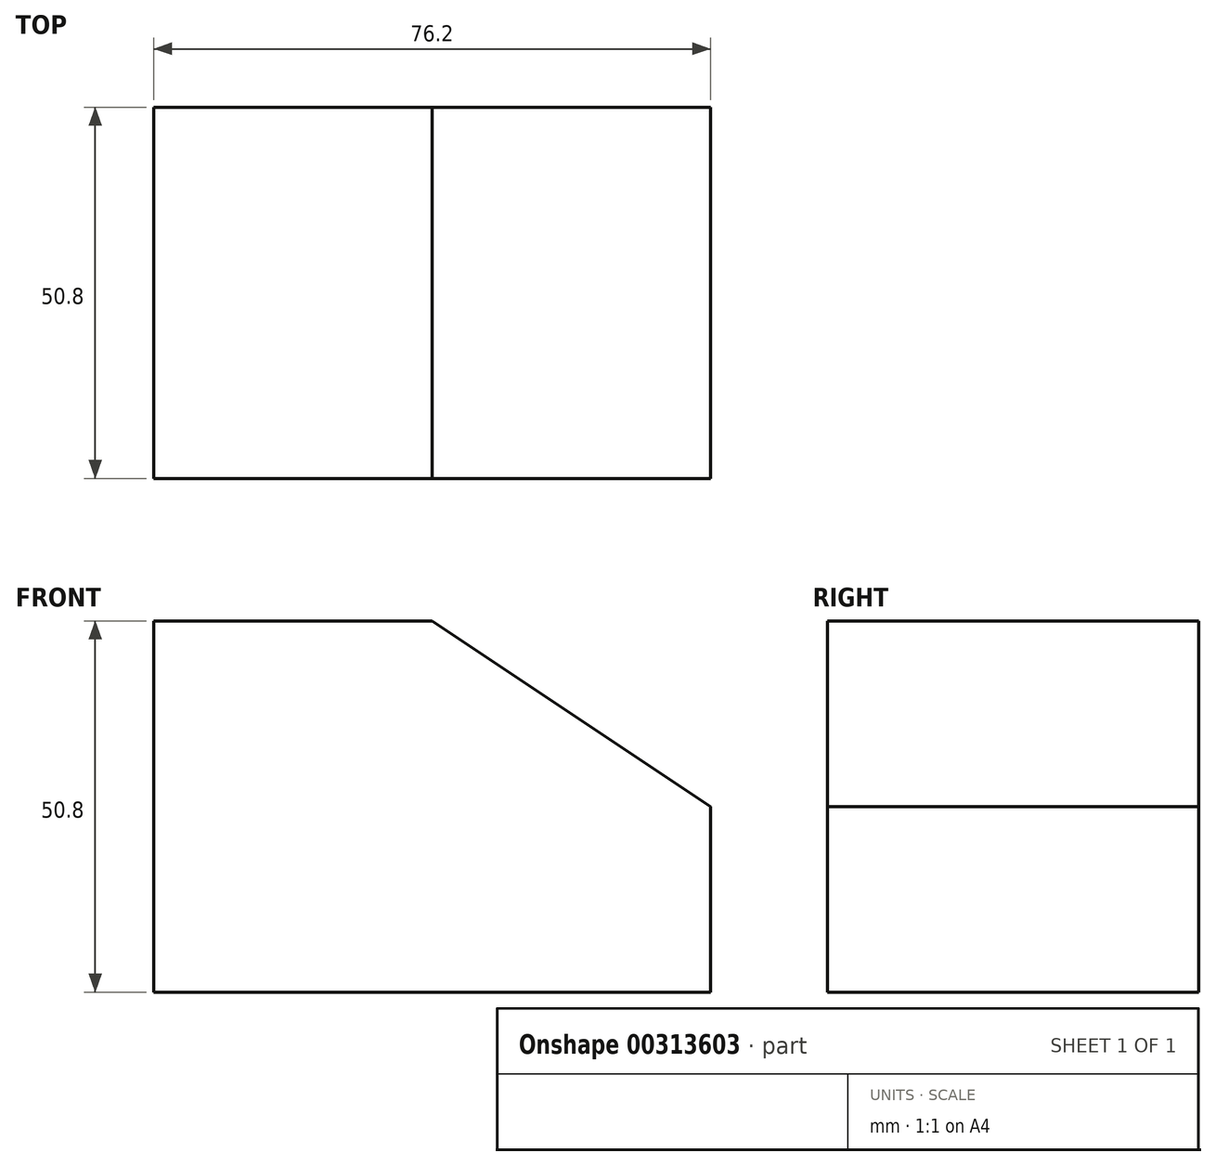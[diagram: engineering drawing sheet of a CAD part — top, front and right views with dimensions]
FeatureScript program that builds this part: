
annotation { "Feature Type Name" : "Feature", "Feature Type Description" : "" }
export const myFeature = defineFeature(function(context is Context, id is Id, definition is map)
    precondition{}
    {
        {
            var Q0;
            Q0=qCreatedBy(makeId("Front.planeOp"),FACE);
            var sketch = newSketch(context, id + "F0", { "sketchPlane" : qUnion([Q0])});
            skLineSegment(sketch, "E0", {"start": v(-22.72, -57.31) * mm, "end": v(53.48, -57.31) * mm});
            skLineSegment(sketch, "E1", {"start": v(-22.72, -57.31) * mm, "end": v(-22.72, -6.51) * mm});
            skLineSegment(sketch, "E2", {"start": v(-22.72, -6.51) * mm, "end": v(15.38, -6.51) * mm});
            skLineSegment(sketch, "E3", {"start": v(53.48, -57.31) * mm, "end": v(53.48, -31.91) * mm});
            skLineSegment(sketch, "E4", {"start": v(15.38, -6.51) * mm, "end": v(53.48, -31.91) * mm});
            skSolve(sketch);
        }
        {
            var Q0;
            Q0=makeQuery(id+"F0.imprint","IMPRINT",FACE,{"disambiguationData":[TD([[makeQuery(id+"F0.imprint","IMPRINT",EDGE,{"derivedFrom":sQuery(id+"F0.wireOp",EDGE,"E0")}),1.0]])]});
            extrude(context, id + "F1", {"entities" : qUnion([Q0]), "depth" : 50.8 * mm});
        }
    });
